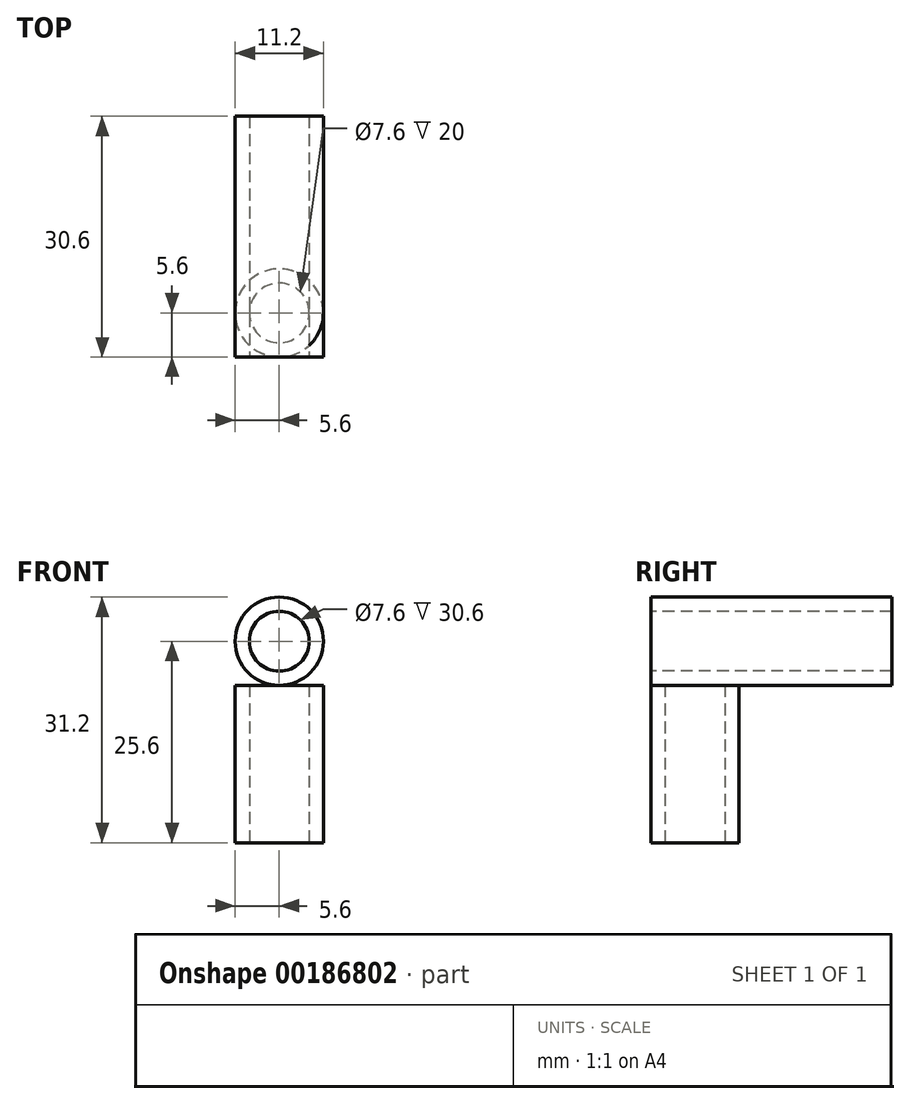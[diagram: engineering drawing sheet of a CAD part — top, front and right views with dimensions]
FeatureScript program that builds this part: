
annotation { "Feature Type Name" : "Feature", "Feature Type Description" : "" }
export const myFeature = defineFeature(function(context is Context, id is Id, definition is map)
    precondition{}
    {
        {
            var Q0;
            Q0=qCreatedBy(makeId("Top.planeOp"),FACE);
            var sketch = newSketch(context, id + "F0", { "sketchPlane" : qUnion([Q0])});
            skCircle(sketch, "E0", {"center": v(0, 0) * mm, "radius": 3.8 * mm});
            skCircle(sketch, "E1", {"center": v(0, 0) * mm, "radius": 5.6 * mm});
            skSolve(sketch);
        }
        {
            var Q0;
            Q0=makeQuery(id+"F0.imprint","IMPRINT",FACE,{"disambiguationData":[TD([[makeQuery(id+"F0.imprint","IMPRINT",EDGE,{"derivedFrom":sQuery(id+"F0.wireOp",EDGE,"E0")}),-1.0]])]});
            extrude(context, id + "F1", {"entities" : qUnion([Q0]), "depth" : 20 * mm});
        }
        {
            var Q0;
            Q0=qCreatedBy(makeId("Front.planeOp"),FACE);
            var sketch = newSketch(context, id + "F2", { "sketchPlane" : qUnion([Q0])});
            skCircle(sketch, "E2", {"center": v(0, 25.6) * mm, "radius": 3.8 * mm});
            skCircle(sketch, "E3", {"center": v(0, 25.6) * mm, "radius": 5.6 * mm});
            skSolve(sketch);
        }
        {
            var Q0;
            Q0 = qSketchRegion(id + "F2", true);
            extrude(context, id + "F3", {"entities" : qUnion([Q0]), "operationType" : NewBodyOperationType.ADD, "oppositeDirection" : true, "depth" : 25 * mm, "hasSecondDirection" : true, "secondDirectionOppositeDirection" : false, "secondDirectionDepth" : 5.6 * mm});
        }
    });
